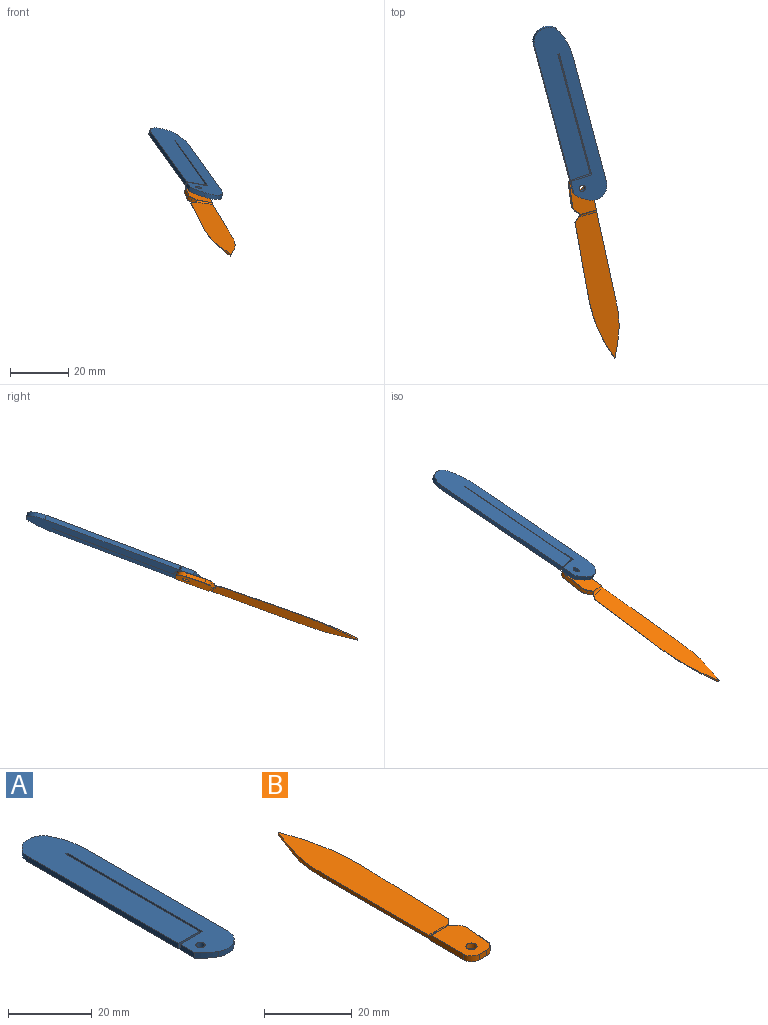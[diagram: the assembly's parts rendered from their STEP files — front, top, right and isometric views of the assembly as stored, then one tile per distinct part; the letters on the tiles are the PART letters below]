
ASSEMBLY  parts=2 mates=1
PART A: 15 faces, bbox 12x65.5x1.6 mm
  f0: plane 50.76x1.59mm, normal (-1,0,0), area 80.6mm2, adj f6,f7,f12,f14
  f1: cylinder r=14.86mm len=4.49mm, axis (0,0,-1), area 9.4mm2, adj f5,f6,f7,f13
  f2: plane 47.67x1.59mm, normal (1,0,0), area 75.7mm2, adj f3,f6,f7,f13
  f3: cylinder r=22.07mm len=9.98mm, axis (0,0,-1), area 16.4mm2, adj f2,f6,f7,f14
  f4: cylinder r=1.1mm len=2.2mm, axis (0,0,-1), area 10.9mm2, adj f6,f7
  f5: plane 4.84x1.59mm, normal (-1,0,0), area 7.7mm2, adj f1,f6,f7,f8
  f6: plane 65.51x12mm, normal (0,0,1), area 717.3mm2, adj f0,f1,f2,f3,f4,f5,f8,f9
  f7: plane 65.51x12mm, normal (0,0,-1), area 717.3mm2, adj f0,f1,f2,f3,f4,f5,f8,f9
  f8: plane 7.62x1.59mm, normal (0,1,0), area 12.1mm2, adj f5,f6,f7,f9
  f9: plane 45.72x1.59mm, normal (-1,0,0), area 72.6mm2, adj f6,f7,f8,f10
  f10: plane 1.59x0.48mm, normal (0,-1,0), area 0.8mm2, adj f6,f7,f9,f11
  f11: plane 45.24x1.59mm, normal (1,0,0), area 71.8mm2, adj f6,f7,f10,f12
  f12: plane 7.14x1.59mm, normal (0,-1,0), area 11.3mm2, adj f0,f6,f7,f11
  f13: cylinder r=5.08mm len=7.5mm, axis (0,0,-1), area 16.7mm2, adj f1,f2,f6,f7
  f14: cylinder r=5.08mm len=9.61mm, axis (0,0,-1), area 21.6mm2, adj f0,f3,f6,f7
PART B: 27 faces, bbox 14.4x67.1x1.6 mm
  f0: plane 13.07x7.91mm, normal (0,0,1), area 89.3mm2, adj f3,f5,f6,f13,f14,f19,f24,f25
  f1: plane 13.07x7.91mm, normal (0,0,-1), area 89.3mm2, adj f4,f5,f6,f15,f16,f21,f24,f25
  f2: plane 6.95x1.4mm, normal (1,-0.08,0), area 9.8mm2, adj f3,f4,f20,f25
  f3: cylinder r=0.1mm len=7.66mm, axis (-0.08,-1,0), area 1.2mm2, adj f0,f2,f19,f25
  f4: cylinder r=0.1mm len=7.66mm, axis (0.08,1,0), area 1.2mm2, adj f1,f2,f21,f25
  f5: plane 44.07x1.61mm, normal (-1,0,0), area 51.2mm2, adj f0,f1,f10,f11,f14,f15,f17,f18
  f6: plane 2.36x1.6mm, normal (-0.02,-1,0), area 3.8mm2, adj f0,f1,f24,f25
  f7: cylinder r=56.03mm len=21.79mm, axis (0,0,-1), area 6.7mm2, adj f9,f10,f11,f22
  f8: plane 2.5x2.5mm, normal (0.71,-0.71,0), area 1.2mm2, adj f9,f10,f11,f12,f13,f16,f17,f18
  f9: plane 29.5x1mm, normal (1,-0.03,0), area 3mm2, adj f7,f8,f10,f11
  f10: plane 53.21x9.11mm, normal (0.05,0,-1), area 404.8mm2, adj f5,f7,f8,f9,f17,f22,f23
  f11: plane 53.21x9.11mm, normal (0.05,0,1), area 404.8mm2, adj f5,f7,f8,f9,f18,f22,f23
  f12: plane 1.52x1.52mm, normal (0.71,0.71,0), area 3mm2, adj f8,f13,f16,f20
  f13: cylinder r=0.1mm len=1.59mm, axis (0.71,-0.71,0), area 0.3mm2, adj f0,f8,f12,f14,f18,f19
  f14: cylinder r=0.1mm len=5.6mm, axis (1,0,0), area 0.5mm2, adj f0,f5,f13,f18
  f15: cylinder r=0.1mm len=5.6mm, axis (-1,0,0), area 0.5mm2, adj f1,f5,f16,f17
  f16: cylinder r=0.1mm len=1.59mm, axis (-0.71,0.71,0), area 0.3mm2, adj f1,f8,f12,f15,f17,f21
  f17: bspline ~12.93x1.02mm, area 5.8mm2, adj f5,f8,f10,f15,f16
  f18: bspline ~13.04x1.03mm, area 5.8mm2, adj f5,f8,f11,f13,f14
  f19: torus R=2.9mm, axis (0,0,1), area 0.4mm2, adj f0,f3,f13,f20
  f20: cylinder r=3mm len=2.36mm, axis (0,0,-1), area 3.6mm2, adj f2,f12,f19,f21
  f21: torus R=2.9mm, axis (0,0,1), area 0.4mm2, adj f1,f4,f16,f20
  f22: cylinder r=0.15mm len=0.67mm, axis (0,0,-1), area 0.1mm2, adj f7,f10,f11,f23
  f23: extruded ~20.41x4.54mm, area 20.3mm2, adj f5,f10,f11,f22
  f24: cylinder r=2.54mm len=2.54mm, axis (0,0,-1), area 6.3mm2, adj f0,f1,f5,f6
  f25: cylinder r=2.54mm len=2.57mm, axis (0,0,-1), area 6mm2, adj f0,f1,f2,f3,f4,f6
  f26: cylinder r=1.27mm len=2.54mm, axis (0,0,-1), area 12.8mm2, adj f0,f1
PLACE A rot(axis=(0.67,0.45,0.6),27.8deg) t=(-37.66,-130.12,168.75)mm
PLACE B rot(axis=(-0.11,0.16,-0.98),166.1deg) t=(-29.97,-105.11,173.34)mm
MATE revolute A.f4 <-> B.f26  axis (-0.25,0.28,-0.93) through (-34,-117.65,171.52)mm
